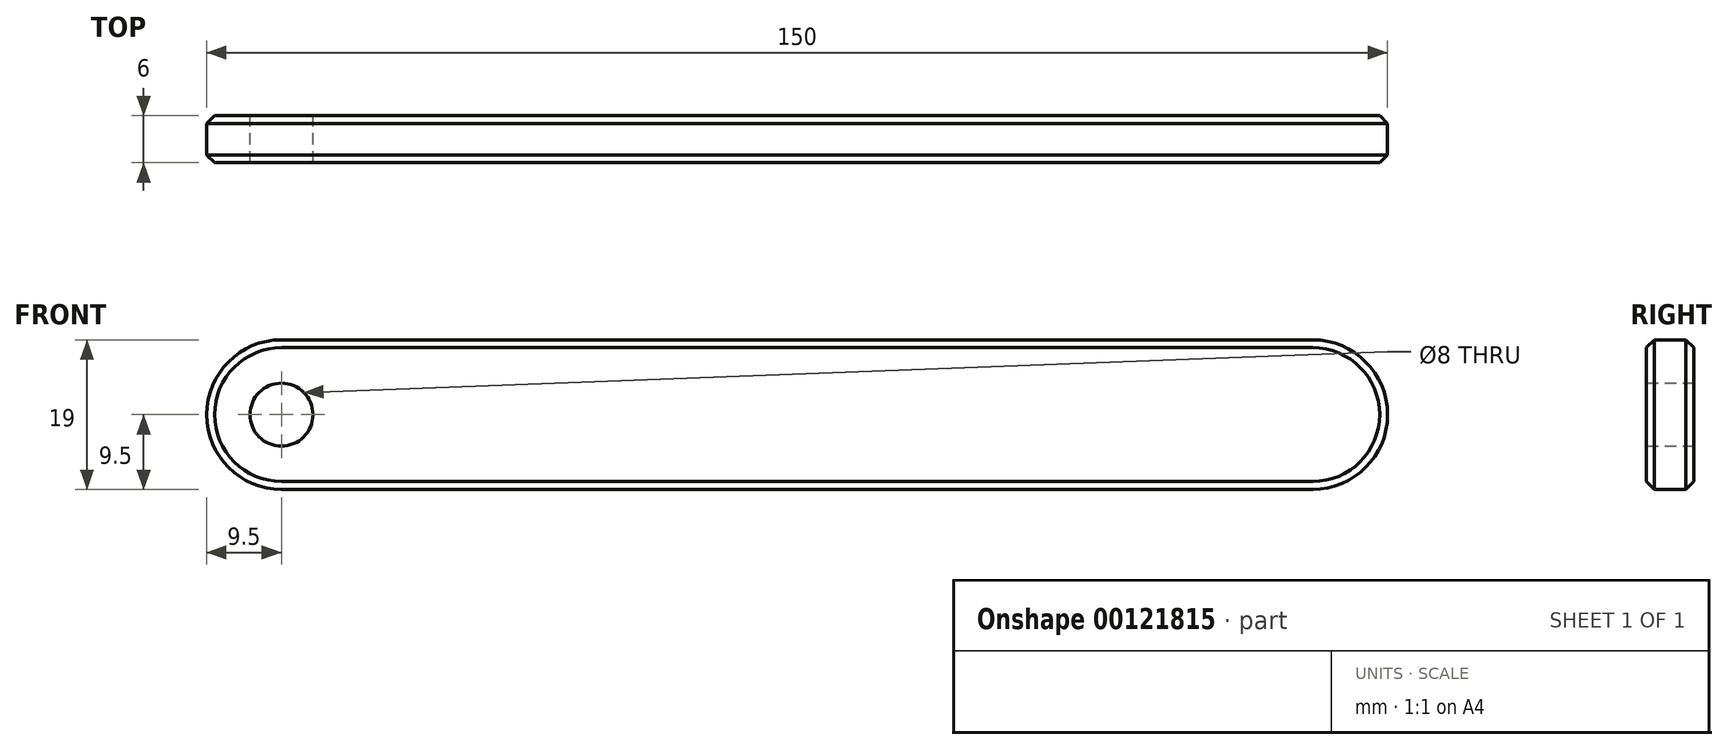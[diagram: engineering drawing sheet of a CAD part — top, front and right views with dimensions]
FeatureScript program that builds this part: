
annotation { "Feature Type Name" : "Feature", "Feature Type Description" : "" }
export const myFeature = defineFeature(function(context is Context, id is Id, definition is map)
    precondition{}
    {
        {
            var Q0;
            Q0=qCreatedBy(makeId("Front.planeOp"),FACE);
            var sketch = newSketch(context, id + "F0", { "sketchPlane" : qUnion([Q0])});
            skPoint(sketch, "E0.middle", {"position": v(0, 0) * mm});
            skPoint(sketch, "E1.endSnap0", {"position": v(75, 0) * mm});
            skCircle(sketch, "E2", {"center": v(-65.5, 0) * mm, "radius": 4 * mm});
            skArc(sketch, "E3", {"start": v(-65.5, 9.5) * mm, "mid": v(-75, 0) * mm, "end": v(-65.5, -9.5) * mm});
            skArc(sketch, "E4", {"start": v(65.5, 9.5) * mm, "mid": v(75, 0) * mm, "end": v(65.5, -9.5) * mm});
            skLineSegment(sketch, "E5", {"start": v(65.5, -9.5) * mm, "end": v(-65.5, -9.5) * mm});
            skLineSegment(sketch, "E6", {"start": v(-65.5, 9.5) * mm, "end": v(65.5, 9.5) * mm});
            skSolve(sketch);
        }
        {
            var Q0;
            Q0 = qSketchRegion(id + "F0", true);
            extrude(context, id + "F1", {"entities" : qUnion([Q0]), "depth" : 6 * mm});
        }
        {
            var Q0;
            Q0=makeQuery(id+"F1.opExtrude","CAP_EDGE",EDGE,{"disambiguationData":[OSD([sQuery(id+"F0.wireOp",EDGE,"E5")])],"isStart":false});
            var Q1;
            Q1=makeQuery(id+"F1.opExtrude","CAP_EDGE",EDGE,{"disambiguationData":[OSD([sQuery(id+"F0.wireOp",EDGE,"E5")])],"isStart":true});
            chamfer(context, id + "F2", {"entities" : qUnion([Q0, Q1]), "width" : 1 * mm, "tangentPropagation" : true});
        }
    });
